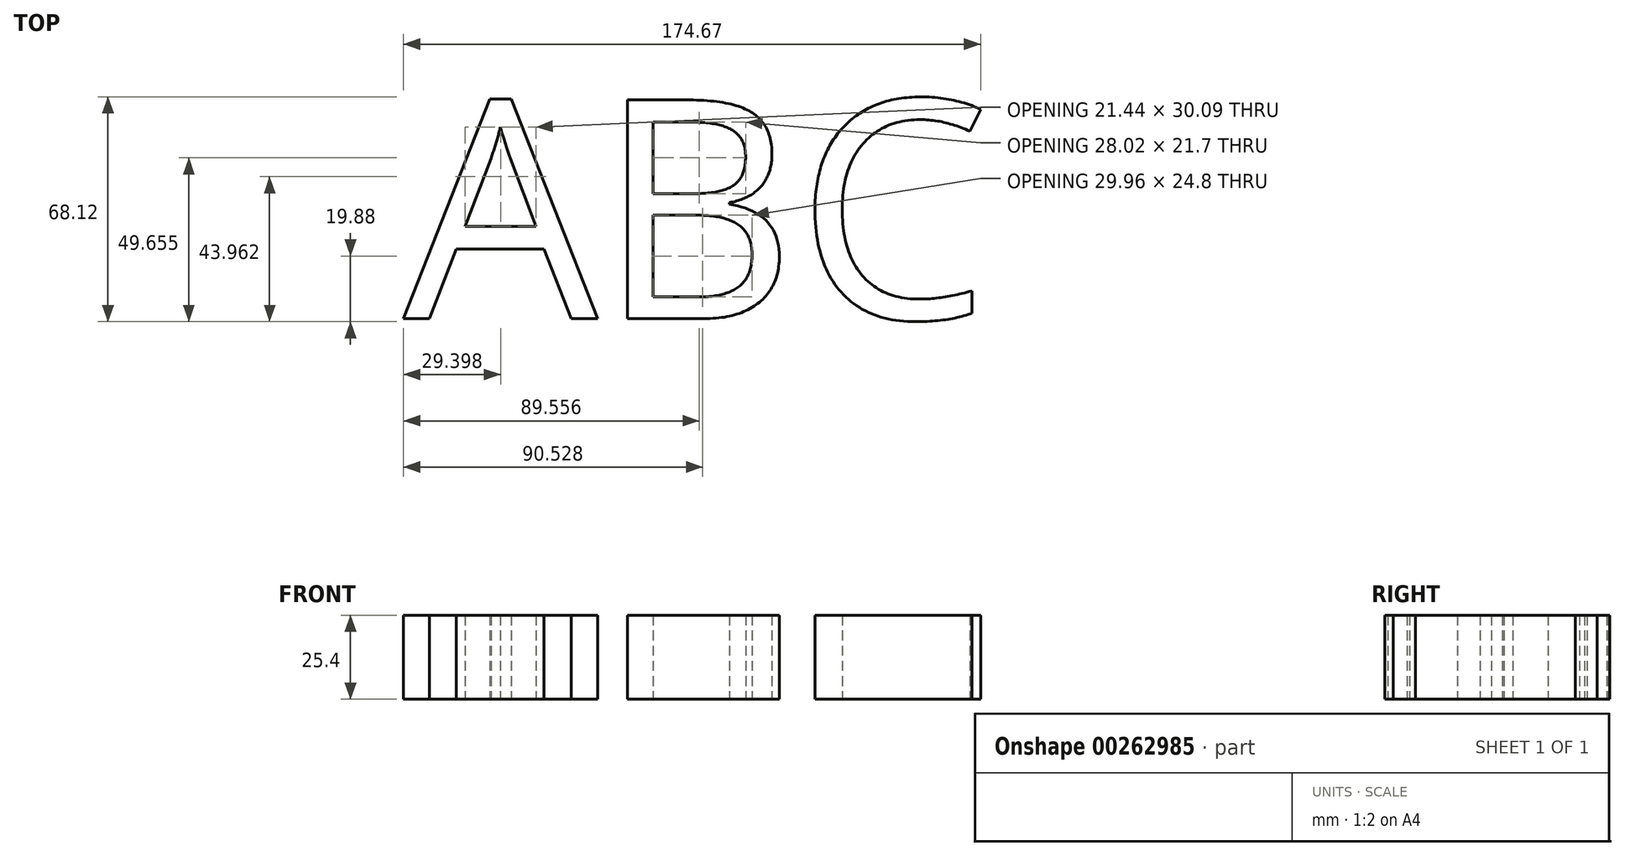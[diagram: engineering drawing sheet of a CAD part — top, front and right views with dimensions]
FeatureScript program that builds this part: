
annotation { "Feature Type Name" : "Feature", "Feature Type Description" : "" }
export const myFeature = defineFeature(function(context is Context, id is Id, definition is map)
    precondition{}
    {
        {
            var Q0;
            Q0=qCreatedBy(makeId("Top.planeOp"),FACE);
            var sketch = newSketch(context, id + "F0", { "sketchPlane" : qUnion([Q0])});
            skText(sketch, "E0", { "text": "ABC", "fontName": "OpenSans-Regular.ttf"});
            const initialGuessF0  = {"E0": [-0.05128, -0.07958, 1, 0, 0.06683]};
            skSetInitialGuess(sketch, initialGuessF0);
            skSolve(sketch);
        }
        {
            var Q0;
            Q0 = qSketchRegion(id + "F0", true);
            extrude(context, id + "F1", {"entities" : qUnion([Q0]), "depth" : 25.4 * mm});
        }
    });
